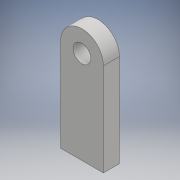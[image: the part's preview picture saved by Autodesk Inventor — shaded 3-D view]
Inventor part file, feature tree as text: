
AUTODESK INVENTOR PART (.ipt)
format: ipt  version: 2018 (Build 220112000, 112)  size: 104,448 bytes
history: native  units: mm
features: extrude x1, sketch x1
ambient origin geometry x8: Origin, YZ Plane, XZ Plane, XY Plane, X Axis, Y Axis, Z Axis, Center Point
bodies: Solid1 (feature_tree)
feature tree (2):
  extrude  "Extrusion1"  Depth=3.0mm
  sketch  "Sketch1"  dims[d0=8.0mm d1=12.0mm d9=8.0mm d10=3.0mm d11=0.0mm d12=3.3mm]
